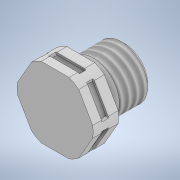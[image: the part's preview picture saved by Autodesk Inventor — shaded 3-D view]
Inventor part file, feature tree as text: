
AUTODESK INVENTOR PART (.ipt)
format: ipt  version: 2021 (Build 250183000, 183)  size: 249,344 bytes
history: native  units: mm
features: extrude x5, sketch x5, shell x1, plane x1, chamfer x1, thread x1, projected_geometry x1
ambient origin geometry x8: Origin, YZ Plane, XZ Plane, XY Plane, X Axis, Y Axis, Z Axis, Center Point
bodies: Solid1 (feature_tree)
feature tree (15):
  extrude  "Extrusion1"  Depth=5.8mm
  shell  "Shell2"  Thickness=5.8mm
  plane  "Work Plane1"
  extrude  "Extrusion2"  [1 undecoded]
  extrude  "Extrusion3"  Depth=10.0mm TaperAngle=360.0deg
  extrude  "Extrusion4"  Depth=10.0mm
  chamfer  "Chamfer1"  Distance=2.0mm
  thread  "Thread1"  [1 undecoded]
  extrude  "Extrusion5"  Depth=2.0mm TaperAngle=45.0deg
  sketch  "Sketch1"  dims[d0=16.0mm d1=17.2mm d2=5.8mm d3=0.0mm]
  sketch  "Sketch2"  dims[d5=0.5mm d6=-2.0mm]
  projected_geometry  "Projected Loop1"
  sketch  "Sketch3"  dims[d7=10.0mm d8=60.0mm d10=360.0deg]
  sketch  "Sketch4"  dims[d12=1.5mm d13=0.0mm d14=10.0mm d15=2.0mm d16=0.0mm d17=11.9mm]
  sketch  "Sketch5"  dims[d18=8.0mm d19=0.0mm d20=0.8mm d21=2.0mm d22=45.0deg d23=11.0mm d24=0.0mm d25=7.0mm d26=10.0mm d27=0.0mm]
note: 2 required parameter values undecoded (feature->parameter linkage not recoverable at this tier; creation-order binding heuristic only, values carry confidence <= 0.55)
